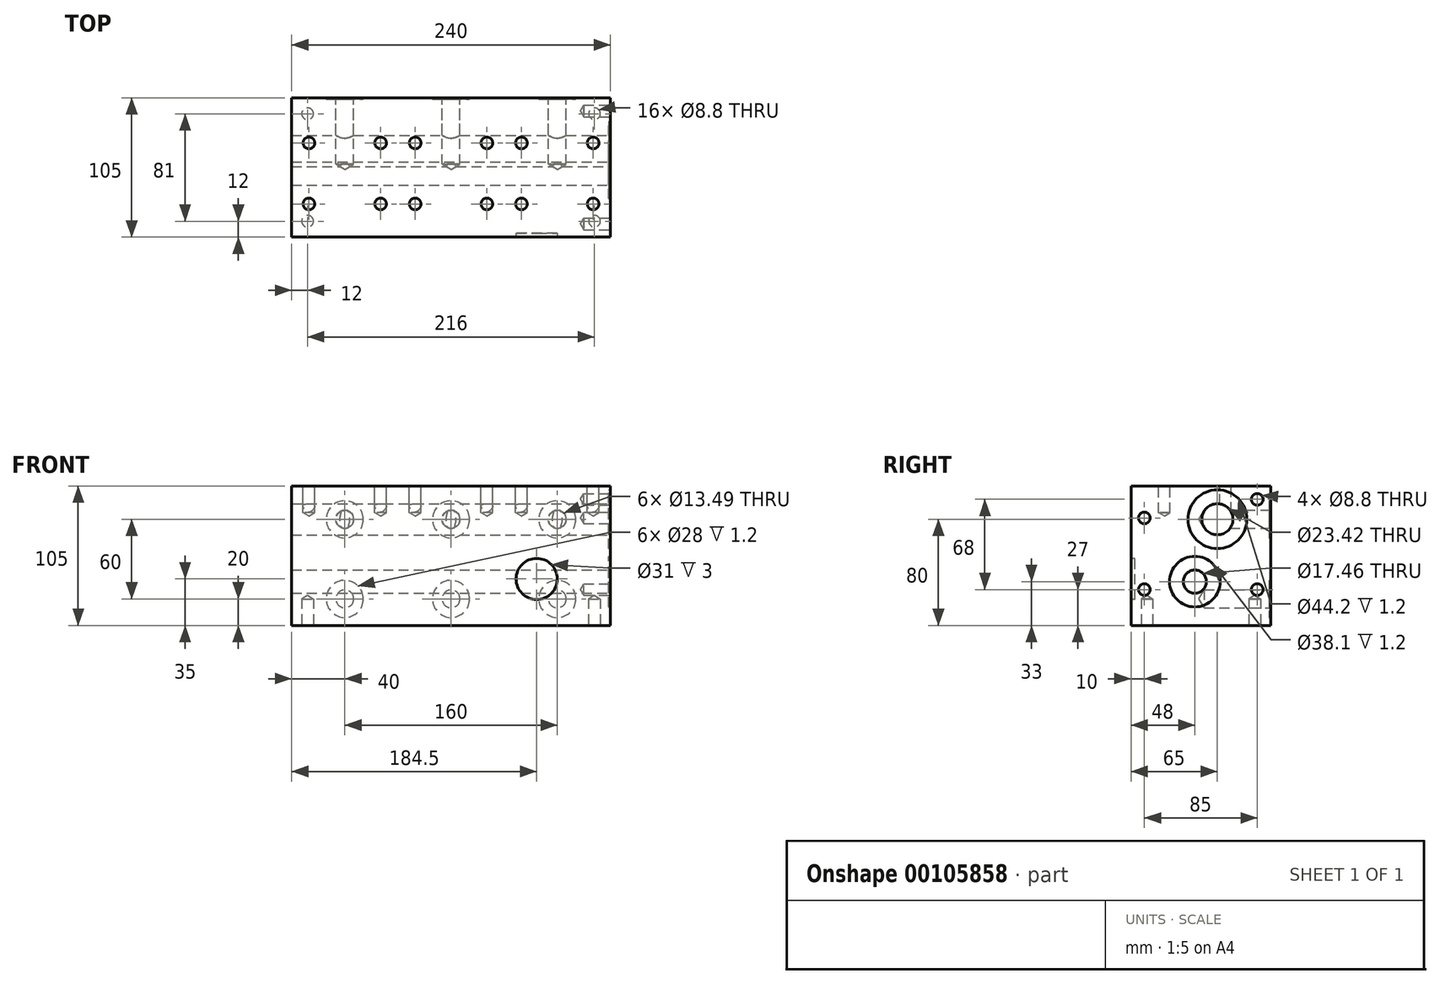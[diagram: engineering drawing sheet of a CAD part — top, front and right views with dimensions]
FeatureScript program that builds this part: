
annotation { "Feature Type Name" : "Feature", "Feature Type Description" : "" }
export const myFeature = defineFeature(function(context is Context, id is Id, definition is map)
    precondition{}
    {
        {
            var Q0;
            Q0=qCreatedBy(makeId("Right.planeOp"),FACE);
            var sketch = newSketch(context, id + "F0", { "sketchPlane" : qUnion([Q0])});
            skLineSegment(sketch, "E0.bottom", {"start": v(-52.5, -52.5) * mm, "end": v(52.5, -52.5) * mm});
            skLineSegment(sketch, "E0.top", {"start": v(-52.5, 52.5) * mm, "end": v(52.5, 52.5) * mm});
            skLineSegment(sketch, "E0.left", {"start": v(-52.5, -52.5) * mm, "end": v(-52.5, 52.5) * mm});
            skLineSegment(sketch, "E0.right", {"start": v(52.5, -52.5) * mm, "end": v(52.5, 52.5) * mm});
            skPoint(sketch, "E0.middle", {"position": v(0, 0) * mm});
            skSolve(sketch);
        }
        {
            var Q0;
            Q0 = qSketchRegion(id + "F0", true);
            extrude(context, id + "F1", {"entities" : qUnion([Q0]), "depth" : 240 * mm});
        }
        {
            var Q0;
            Q0=makeQuery(id+"F1.opExtrude","CAP_FACE",FACE,{"disambiguationData":[OSD([sQuery(id+"F0.wireOp",EDGE,"E0.bottom"),sQuery(id+"F0.wireOp",EDGE,"E0.top"),sQuery(id+"F0.wireOp",EDGE,"E0.left"),sQuery(id+"F0.wireOp",EDGE,"E0.right")])],"isStart":false});
            var sketch = newSketch(context, id + "F2", { "sketchPlane" : qUnion([Q0])});
            skPoint(sketch, "E1", {"position": v(12.5, 27.5) * mm});
            skPoint(sketch, "E2", {"position": v(-4.5, -19.5) * mm});
            skPoint(sketch, "E3", {"position": v(-42.5, -25.5) * mm});
            skPoint(sketch, "E4", {"position": v(-42.5, 28.5) * mm});
            skPoint(sketch, "E5", {"position": v(42.5, -25.5) * mm});
            skPoint(sketch, "E6", {"position": v(42.5, 42.5) * mm});
            skCircle(sketch, "E7", {"center": v(-4.5, -19.5) * mm, "radius": 19.05 * mm});
            skCircle(sketch, "E8", {"center": v(12.5, 27.5) * mm, "radius": 22.1 * mm});
            skSolve(sketch);
        }
        {
            var Q0;
            Q0=sQuery(id+"F2.wireOp",VERTEX,"E4");
            var Q1;
            Q1=sQuery(id+"F2.wireOp",VERTEX,"E6");
            var Q2;
            Q2=sQuery(id+"F2.wireOp",VERTEX,"E5");
            var Q3;
            Q3=sQuery(id+"F2.wireOp",VERTEX,"E3");
            var Q4;
            Q4=makeQuery(id+"F1.opExtrude","SWEPT_BODY",BODY,{"disambiguationData":[OSD([sQuery(id+"F0.wireOp",EDGE,"E0.bottom"),sQuery(id+"F0.wireOp",EDGE,"E0.top"),sQuery(id+"F0.wireOp",EDGE,"E0.left"),sQuery(id+"F0.wireOp",EDGE,"E0.right")])]});
            hole(context, id + "F3", {"style" : HoleStyle.SIMPLE, "endStyle" : HoleEndStyle.BLIND, "standardTappedOrClearance" : lookupTablePath({ "standard" : "ISO", "engagement" : "75%", "pitch" : "1.25 mm", "size" : "M10", "type" : "Tapped" }), "standardBlindInLast" : lookupTablePath({ "standard" : "ISO", "engagement" : "75%", "pitch" : "1.25 mm", "size" : "M10", "type" : "Tapped" }), "holeDiameter" : 8.8 * mm, "holeDepth" : 20 * mm, "locations" : qUnion([Q0, Q1, Q2, Q3]), "scope" : qUnion([Q4]), "majorDiameter" : 10 * mm});
        }
        {
            var Q0;
            Q0=sQuery(id+"F2.wireOp",VERTEX,"E2");
            var Q1;
            Q1=makeQuery(id+"F1.opExtrude","SWEPT_BODY",BODY,{"disambiguationData":[OSD([sQuery(id+"F0.wireOp",EDGE,"E0.bottom"),sQuery(id+"F0.wireOp",EDGE,"E0.top"),sQuery(id+"F0.wireOp",EDGE,"E0.left"),sQuery(id+"F0.wireOp",EDGE,"E0.right")])]});
            hole(context, id + "F4", {"style" : HoleStyle.SIMPLE, "endStyle" : HoleEndStyle.THROUGH, "standardTappedOrClearance" : lookupTablePath({ "standard" : "ANSI", "engagement" : "75%", "pitch" : "16 tpi", "size" : "3/4", "type" : "Tapped" }), "standardBlindInLast" : lookupTablePath({ "standard" : "ANSI", "engagement" : "75%", "pitch" : "16 tpi", "size" : "3/4", "type" : "Tapped" }), "holeDiameter" : 17.46 * mm, "locations" : qUnion([Q0]), "scope" : qUnion([Q1]), "isTappedThrough" : true, "majorDiameter" : 19.05 * mm, "showTappedDepth" : true});
        }
        {
            var Q0;
            Q0=sQuery(id+"F2.wireOp",VERTEX,"E1");
            var Q1;
            Q1=makeQuery(id+"F1.opExtrude","SWEPT_BODY",BODY,{"disambiguationData":[OSD([sQuery(id+"F0.wireOp",EDGE,"E0.bottom"),sQuery(id+"F0.wireOp",EDGE,"E0.top"),sQuery(id+"F0.wireOp",EDGE,"E0.left"),sQuery(id+"F0.wireOp",EDGE,"E0.right")])]});
            hole(context, id + "F5", {"style" : HoleStyle.SIMPLE, "endStyle" : HoleEndStyle.THROUGH, "standardTappedOrClearance" : lookupTablePath({ "standard" : "ANSI", "engagement" : "75%", "pitch" : "12 tpi", "size" : "1", "type" : "Tapped" }), "standardBlindInLast" : lookupTablePath({ "standard" : "ANSI", "engagement" : "75%", "pitch" : "12 tpi", "size" : "1", "type" : "Tapped" }), "holeDiameter" : 23.42 * mm, "locations" : qUnion([Q0]), "scope" : qUnion([Q1]), "isTappedThrough" : true, "majorDiameter" : 25.4 * mm, "showTappedDepth" : true});
        }
        {
            var Q0;
            Q0 = qSketchRegion(id + "F2", true);
            extrude(context, id + "F6", {"entities" : qUnion([Q0]), "operationType" : NewBodyOperationType.REMOVE, "oppositeDirection" : true, "depth" : 1.2 * mm});
        }
        {
            var Q0;
            Q0=makeQuery(id+"F1.opExtrude","SWEPT_FACE",FACE,{"disambiguationData":[OSD([sQuery(id+"F0.wireOp",EDGE,"E0.right")])]});
            var sketch = newSketch(context, id + "F7", { "sketchPlane" : qUnion([Q0])});
            skPoint(sketch, "E9", {"position": v(-200, 27.5) * mm});
            skPoint(sketch, "E10", {"position": v(-200, -32.5) * mm});
            skPoint(sketch, "E11.1.0.0", {"position": v(-120, 27.5) * mm});
            skPoint(sketch, "E11.1.0.1", {"position": v(-120, -32.5) * mm});
            skPoint(sketch, "E11.2.0.0", {"position": v(-40, 27.5) * mm});
            skPoint(sketch, "E11.2.0.1", {"position": v(-40, -32.5) * mm});
            skPoint(sketch, "E11.3.0.0", {"position": v(40, 27.5) * mm});
            skPoint(sketch, "E11.3.0.1", {"position": v(40, -32.5) * mm});
            skPoint(sketch, "E11.4.0.0", {"position": v(120, 27.5) * mm});
            skPoint(sketch, "E11.4.0.1", {"position": v(120, -32.5) * mm});
            skPoint(sketch, "E11.5.0.0", {"position": v(200, 27.5) * mm});
            skPoint(sketch, "E11.5.0.1", {"position": v(200, -32.5) * mm});
            skPoint(sketch, "E11.6.0.0", {"position": v(280, 27.5) * mm});
            skPoint(sketch, "E11.6.0.1", {"position": v(280, -32.5) * mm});
            skLineSegment(sketch, "E11.direction1", {"start": v(-200, 27.5) * mm, "end": v(-120, 27.5) * mm, "construction": true});
            skCircle(sketch, "E12", {"center": v(-200, 27.5) * mm, "radius": 14 * mm});
            skCircle(sketch, "E13.0.1.0", {"center": v(-200, -32.5) * mm, "radius": 14 * mm});
            skCircle(sketch, "E13.1.0.0", {"center": v(-120, 27.5) * mm, "radius": 14 * mm});
            skCircle(sketch, "E13.1.1.0", {"center": v(-120, -32.5) * mm, "radius": 14 * mm});
            skCircle(sketch, "E13.2.0.0", {"center": v(-40, 27.5) * mm, "radius": 14 * mm});
            skCircle(sketch, "E13.2.1.0", {"center": v(-40, -32.5) * mm, "radius": 14 * mm});
            skCircle(sketch, "E13.3.0.0", {"center": v(40, 27.5) * mm, "radius": 14 * mm});
            skCircle(sketch, "E13.3.1.0", {"center": v(40, -32.5) * mm, "radius": 14 * mm});
            skCircle(sketch, "E13.4.0.0", {"center": v(120, 27.5) * mm, "radius": 14 * mm});
            skCircle(sketch, "E13.4.1.0", {"center": v(120, -32.5) * mm, "radius": 14 * mm});
            skCircle(sketch, "E13.5.0.0", {"center": v(200, 27.5) * mm, "radius": 14 * mm});
            skCircle(sketch, "E13.5.1.0", {"center": v(200, -32.5) * mm, "radius": 14 * mm});
            skCircle(sketch, "E13.6.0.0", {"center": v(280, 27.5) * mm, "radius": 14 * mm});
            skCircle(sketch, "E13.6.1.0", {"center": v(280, -32.5) * mm, "radius": 14 * mm});
            skLineSegment(sketch, "E13.direction2", {"start": v(-200, 27.5) * mm, "end": v(-200, -32.5) * mm, "construction": true});
            skSolve(sketch);
        }
        {
            var Q0;
            Q0=sQuery(id+"F7.wireOp",VERTEX,"E9");
            var Q1;
            Q1=sQuery(id+"F7.wireOp",VERTEX,"E10");
            var Q2;
            Q2=sQuery(id+"F7.wireOp",VERTEX,"E11.1.0.1");
            var Q3;
            Q3=sQuery(id+"F7.wireOp",VERTEX,"E11.1.0.0");
            var Q4;
            Q4=sQuery(id+"F7.wireOp",VERTEX,"E11.2.0.0");
            var Q5;
            Q5=sQuery(id+"F7.wireOp",VERTEX,"E11.2.0.1");
            var Q6;
            Q6=sQuery(id+"F7.wireOp",VERTEX,"E11.3.0.1");
            var Q7;
            Q7=sQuery(id+"F7.wireOp",VERTEX,"E11.3.0.0");
            var Q8;
            Q8=sQuery(id+"F7.wireOp",VERTEX,"E11.4.0.0");
            var Q9;
            Q9=sQuery(id+"F7.wireOp",VERTEX,"E11.4.0.1");
            var Q10;
            Q10=sQuery(id+"F7.wireOp",VERTEX,"E11.5.0.1");
            var Q11;
            Q11=sQuery(id+"F7.wireOp",VERTEX,"E11.5.0.0");
            var Q12;
            Q12=sQuery(id+"F7.wireOp",VERTEX,"E11.6.0.0");
            var Q13;
            Q13=sQuery(id+"F7.wireOp",VERTEX,"E11.6.0.1");
            var Q14;
            Q14=makeQuery(id+"F1.opExtrude","SWEPT_BODY",BODY,{"disambiguationData":[OSD([sQuery(id+"F0.wireOp",EDGE,"E0.bottom"),sQuery(id+"F0.wireOp",EDGE,"E0.top"),sQuery(id+"F0.wireOp",EDGE,"E0.left"),sQuery(id+"F0.wireOp",EDGE,"E0.right")])]});
            hole(context, id + "F8", {"style" : HoleStyle.SIMPLE, "endStyle" : HoleEndStyle.BLIND, "standardTappedOrClearance" : lookupTablePath({ "standard" : "ANSI", "fit" : "Normal (ASME)", "size" : "1/2", "type" : "Clearance" }), "standardBlindInLast" : lookupTablePath({ "fit" : "Free", "standard" : "ANSI", "size" : "1/2", "type" : "Clearance" }), "holeDiameter" : 13.5 * mm, "holeDepth" : 50 * mm, "locations" : qUnion([Q0, Q1, Q2, Q3, Q4, Q5, Q6, Q7, Q8, Q9, Q10, Q11, Q12, Q13]), "scope" : qUnion([Q14])});
        }
        {
            var Q0;
            Q0 = qSketchRegion(id + "F7", true);
            extrude(context, id + "F9", {"entities" : qUnion([Q0]), "operationType" : NewBodyOperationType.REMOVE, "oppositeDirection" : true, "depth" : 1.2 * mm});
        }
        {
            var Q0;
            Q0=makeQuery(id+"F1.opExtrude","SWEPT_FACE",FACE,{"disambiguationData":[OSD([sQuery(id+"F0.wireOp",EDGE,"E0.top")])]});
            var sketch = newSketch(context, id + "F10", { "sketchPlane" : qUnion([Q0])});
            skPoint(sketch, "E14", {"position": v(13, 18.5) * mm});
            skPoint(sketch, "E15", {"position": v(67, 18.5) * mm});
            skPoint(sketch, "E16", {"position": v(13, -27.5) * mm});
            skPoint(sketch, "E17", {"position": v(67, -27.5) * mm});
            skPoint(sketch, "E18.1.0.0", {"position": v(93, 18.5) * mm});
            skPoint(sketch, "E18.1.0.1", {"position": v(93, -27.5) * mm});
            skPoint(sketch, "E18.1.0.2", {"position": v(147, -27.5) * mm});
            skPoint(sketch, "E18.1.0.3", {"position": v(147, 18.5) * mm});
            skPoint(sketch, "E18.2.0.0", {"position": v(173, 18.5) * mm});
            skPoint(sketch, "E18.2.0.1", {"position": v(173, -27.5) * mm});
            skPoint(sketch, "E18.2.0.2", {"position": v(227, -27.5) * mm});
            skPoint(sketch, "E18.2.0.3", {"position": v(227, 18.5) * mm});
            skLineSegment(sketch, "E18.direction1", {"start": v(13, 18.5) * mm, "end": v(93, 18.5) * mm, "construction": true});
            skSolve(sketch);
        }
        {
            var Q0;
            Q0=sQuery(id+"F10.wireOp",VERTEX,"E14");
            var Q1;
            Q1=sQuery(id+"F10.wireOp",VERTEX,"E16");
            var Q2;
            Q2=sQuery(id+"F10.wireOp",VERTEX,"E17");
            var Q3;
            Q3=sQuery(id+"F10.wireOp",VERTEX,"E15");
            var Q4;
            Q4=sQuery(id+"F10.wireOp",VERTEX,"E18.1.0.0");
            var Q5;
            Q5=sQuery(id+"F10.wireOp",VERTEX,"E18.1.0.1");
            var Q6;
            Q6=sQuery(id+"F10.wireOp",VERTEX,"E18.1.0.3");
            var Q7;
            Q7=sQuery(id+"F10.wireOp",VERTEX,"E18.1.0.2");
            var Q8;
            Q8=sQuery(id+"F10.wireOp",VERTEX,"E18.2.0.1");
            var Q9;
            Q9=sQuery(id+"F10.wireOp",VERTEX,"E18.2.0.0");
            var Q10;
            Q10=sQuery(id+"F10.wireOp",VERTEX,"E18.2.0.3");
            var Q11;
            Q11=sQuery(id+"F10.wireOp",VERTEX,"E18.2.0.2");
            var Q12;
            Q12=sQuery(id+"F10.wireOp",VERTEX,"E18.3.0.1");
            var Q13;
            Q13=sQuery(id+"F10.wireOp",VERTEX,"E18.3.0.0");
            var Q14;
            Q14=sQuery(id+"F10.wireOp",VERTEX,"E18.3.0.3");
            var Q15;
            Q15=sQuery(id+"F10.wireOp",VERTEX,"E18.3.0.2");
            var Q16;
            Q16=sQuery(id+"F10.wireOp",VERTEX,"E18.4.0.1");
            var Q17;
            Q17=sQuery(id+"F10.wireOp",VERTEX,"E18.4.0.0");
            var Q18;
            Q18=sQuery(id+"F10.wireOp",VERTEX,"E18.4.0.3");
            var Q19;
            Q19=sQuery(id+"F10.wireOp",VERTEX,"E18.4.0.2");
            var Q20;
            Q20=sQuery(id+"F10.wireOp",VERTEX,"E18.5.0.1");
            var Q21;
            Q21=sQuery(id+"F10.wireOp",VERTEX,"E18.5.0.0");
            var Q22;
            Q22=sQuery(id+"F10.wireOp",VERTEX,"E18.5.0.3");
            var Q23;
            Q23=sQuery(id+"F10.wireOp",VERTEX,"E18.6.0.0");
            var Q24;
            Q24=sQuery(id+"F10.wireOp",VERTEX,"E18.5.0.2");
            var Q25;
            Q25=sQuery(id+"F10.wireOp",VERTEX,"E18.6.0.1");
            var Q26;
            Q26=sQuery(id+"F10.wireOp",VERTEX,"E18.6.0.3");
            var Q27;
            Q27=sQuery(id+"F10.wireOp",VERTEX,"E18.6.0.2");
            var Q28;
            Q28=makeQuery(id+"F1.opExtrude","SWEPT_BODY",BODY,{"disambiguationData":[OSD([sQuery(id+"F0.wireOp",EDGE,"E0.bottom"),sQuery(id+"F0.wireOp",EDGE,"E0.top"),sQuery(id+"F0.wireOp",EDGE,"E0.left"),sQuery(id+"F0.wireOp",EDGE,"E0.right")])]});
            hole(context, id + "F11", {"style" : HoleStyle.SIMPLE, "endStyle" : HoleEndStyle.BLIND, "standardTappedOrClearance" : lookupTablePath({ "standard" : "ISO", "engagement" : "75%", "pitch" : "1.25 mm", "size" : "M10", "type" : "Tapped" }), "standardBlindInLast" : lookupTablePath({ "standard" : "ISO", "engagement" : "75%", "pitch" : "1.25 mm", "size" : "M10", "type" : "Tapped" }), "holeDiameter" : 8.8 * mm, "holeDepth" : 20 * mm, "locations" : qUnion([Q0, Q1, Q2, Q3, Q4, Q5, Q6, Q7, Q8, Q9, Q10, Q11, Q12, Q13, Q14, Q15, Q16, Q17, Q18, Q19, Q20, Q21, Q22, Q23, Q24, Q25, Q26, Q27]), "scope" : qUnion([Q28]), "majorDiameter" : 10 * mm});
        }
        {
            var Q0;
            Q0=makeQuery(id+"F1.opExtrude","SWEPT_FACE",FACE,{"disambiguationData":[OSD([sQuery(id+"F0.wireOp",EDGE,"E0.bottom")])]});
            var sketch = newSketch(context, id + "F12", { "sketchPlane" : qUnion([Q0])});
            skPoint(sketch, "E19", {"position": v(12, 40.5) * mm});
            skPoint(sketch, "E20", {"position": v(12, -40.5) * mm});
            skPoint(sketch, "E21", {"position": v(228, 40.5) * mm});
            skPoint(sketch, "E22", {"position": v(228, -40.5) * mm});
            skSolve(sketch);
        }
        {
            var Q0;
            Q0=sQuery(id+"F12.wireOp",VERTEX,"E19");
            var Q1;
            Q1=sQuery(id+"F12.wireOp",VERTEX,"E20");
            var Q2;
            Q2=sQuery(id+"F12.wireOp",VERTEX,"E22");
            var Q3;
            Q3=sQuery(id+"F12.wireOp",VERTEX,"E21");
            var Q4;
            Q4=makeQuery(id+"F1.opExtrude","SWEPT_BODY",BODY,{"disambiguationData":[OSD([sQuery(id+"F0.wireOp",EDGE,"E0.bottom"),sQuery(id+"F0.wireOp",EDGE,"E0.top"),sQuery(id+"F0.wireOp",EDGE,"E0.left"),sQuery(id+"F0.wireOp",EDGE,"E0.right")])]});
            hole(context, id + "F13", {"style" : HoleStyle.SIMPLE, "endStyle" : HoleEndStyle.BLIND, "standardTappedOrClearance" : lookupTablePath({ "standard" : "ISO", "fit" : "Normal", "size" : "M8", "type" : "Clearance" }), "standardBlindInLast" : lookupTablePath({ "fit" : "Standard", "standard" : "ISO", "size" : "M8", "type" : "Clearance" }), "holeDiameter" : 8.8 * mm, "holeDepth" : 20 * mm, "locations" : qUnion([Q0, Q1, Q2, Q3]), "scope" : qUnion([Q4])});
        }
        {
            var Q0;
            Q0=makeQuery(id+"F1.opExtrude","SWEPT_FACE",FACE,{"disambiguationData":[OSD([sQuery(id+"F0.wireOp",EDGE,"E0.left")])]});
            var sketch = newSketch(context, id + "F14", { "sketchPlane" : qUnion([Q0])});
            skCircle(sketch, "E23", {"center": v(184.5, -17.5) * mm, "radius": 15.5 * mm});
            skSolve(sketch);
        }
        {
            var Q0;
            Q0 = qSketchRegion(id + "F14", true);
            extrude(context, id + "F15", {"entities" : qUnion([Q0]), "operationType" : NewBodyOperationType.REMOVE, "oppositeDirection" : true, "depth" : 3 * mm});
        }
    });
